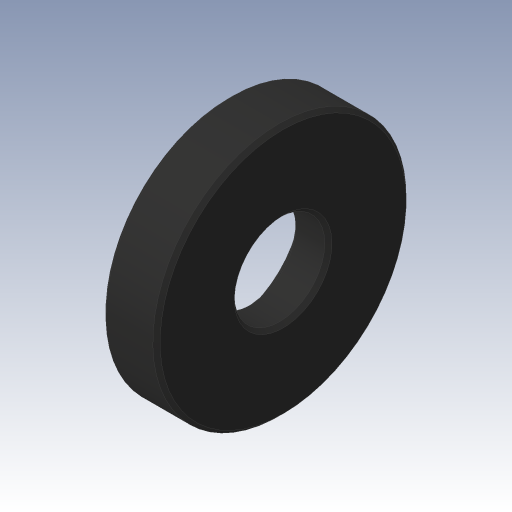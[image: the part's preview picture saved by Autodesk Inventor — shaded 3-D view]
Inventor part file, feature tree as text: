
AUTODESK INVENTOR PART (.ipt)
format: ipt  version: 2023.3 (Build 273359000, 359)  size: 150,528 bytes
history: native  units: in
note: dims shown in document units (in); Inventor stores cm internally (conversion verified against a paired STEP export)
features: revolve x1, chamfer x1, sketch x1
ambient origin geometry x8: Origin, YZ Plane, XZ Plane, XY Plane, X Axis, Y Axis, Z Axis, Center Point
bodies: Body1 (feature_tree)
feature tree (3):
  revolve  "Umdrehung1"
  chamfer  "Fase1"  Distance=0.1969in
  sketch  "Skizze3"  dims[d4=0.5512in d5=0.1969in d6=0.1181in d7=0.0394in d9=0.315in d10=90.0deg d11=0.0079in d12=0.0787in d13=45.0deg]
